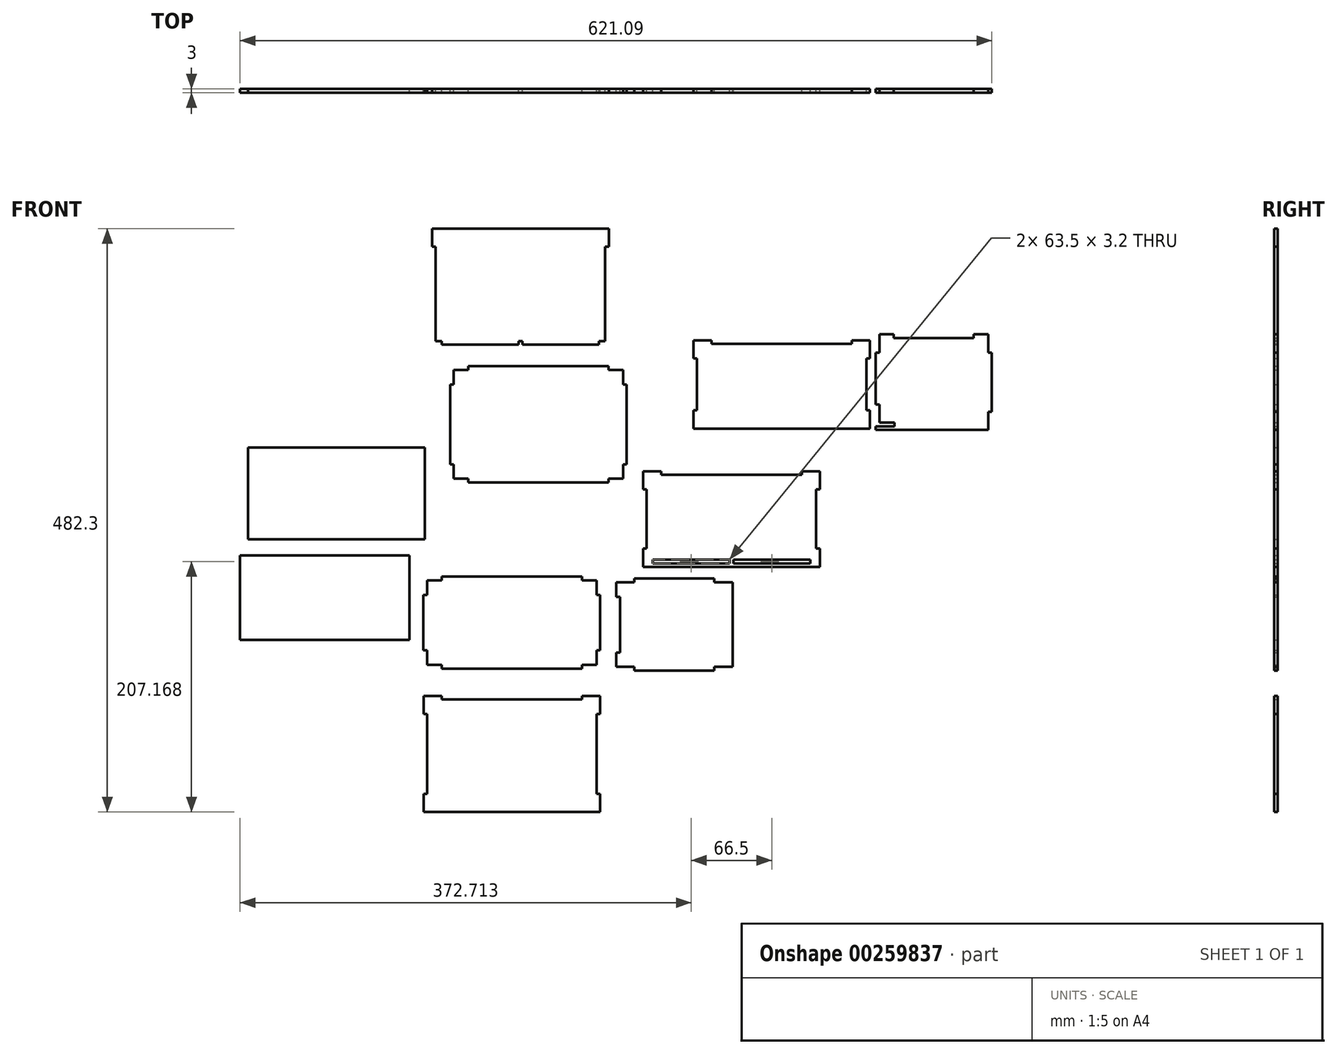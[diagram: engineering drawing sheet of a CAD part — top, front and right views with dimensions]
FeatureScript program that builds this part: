
annotation { "Feature Type Name" : "Feature", "Feature Type Description" : "" }
export const myFeature = defineFeature(function(context is Context, id is Id, definition is map)
    precondition{}
    {
        {
            var Q0;
            Q0=qCreatedBy(makeId("Front.planeOp"),FACE);
            var sketch = newSketch(context, id + "F0", { "sketchPlane" : qUnion([Q0])});
            skLineSegment(sketch, "E0.bottom", {"start": v(-79.7, 20.87) * mm, "end": v(60.3, 20.87) * mm});
            skLineSegment(sketch, "E0.top", {"start": v(-79.7, -49.13) * mm, "end": v(60.3, -49.13) * mm});
            skLineSegment(sketch, "E0.left", {"start": v(-79.7, 20.87) * mm, "end": v(-79.7, -49.13) * mm});
            skLineSegment(sketch, "E0.right", {"start": v(60.3, 20.87) * mm, "end": v(60.3, -49.13) * mm});
            skSolve(sketch);
        }
        {
            var Q0;
            Q0 = qSketchRegion(id + "F0", true);
            extrude(context, id + "F1", {"entities" : qUnion([Q0]), "depth" : 3 * mm});
        }
        {
            var Q0;
            Q0=qCreatedBy(makeId("Front.planeOp"),FACE);
            var sketch = newSketch(context, id + "F2", { "sketchPlane" : qUnion([Q0])});
            skLineSegment(sketch, "E1.bottom", {"start": v(-73.11, 34.1) * mm, "end": v(72.89, 34.1) * mm});
            skLineSegment(sketch, "E1.top", {"start": v(-73.11, 110.1) * mm, "end": v(72.89, 110.1) * mm});
            skLineSegment(sketch, "E1.left", {"start": v(-73.11, 34.1) * mm, "end": v(-73.11, 110.1) * mm});
            skLineSegment(sketch, "E1.right", {"start": v(72.89, 34.1) * mm, "end": v(72.89, 110.1) * mm});
            skSolve(sketch);
        }
        {
            var Q0;
            Q0 = qSketchRegion(id + "F2", true);
            extrude(context, id + "F3", {"entities" : qUnion([Q0]), "depth" : 3 * mm});
        }
        {
            var Q0;
            Q0=qCreatedBy(makeId("Front.planeOp"),FACE);
            var sketch = newSketch(context, id + "F4", { "sketchPlane" : qUnion([Q0])});
            skLineSegment(sketch, "E2.bottom", {"start": v(86.8, 3.27) * mm, "end": v(202.8, 3.27) * mm});
            skLineSegment(sketch, "E2.top", {"start": v(86.8, -72.73) * mm, "end": v(202.8, -72.73) * mm});
            skLineSegment(sketch, "E2.left", {"start": v(71.8, -11.73) * mm, "end": v(71.8, -57.73) * mm});
            skLineSegment(sketch, "E2.right", {"start": v(217.8, -11.73) * mm, "end": v(217.8, -57.73) * mm});
            skLineSegment(sketch, "E3", {"start": v(71.8, -11.73) * mm, "end": v(74.8, -11.73) * mm});
            skLineSegment(sketch, "E4", {"start": v(74.8, -11.73) * mm, "end": v(74.8, 0.27) * mm});
            skLineSegment(sketch, "E5", {"start": v(74.8, 0.27) * mm, "end": v(86.8, 0.27) * mm});
            skLineSegment(sketch, "E6", {"start": v(86.8, 0.27) * mm, "end": v(86.8, 3.27) * mm});
            skLineSegment(sketch, "E7", {"start": v(71.8, -57.73) * mm, "end": v(74.8, -57.73) * mm});
            skLineSegment(sketch, "E8", {"start": v(74.8, -57.73) * mm, "end": v(74.8, -69.73) * mm});
            skLineSegment(sketch, "E9", {"start": v(74.8, -69.73) * mm, "end": v(86.8, -69.73) * mm});
            skLineSegment(sketch, "E10", {"start": v(86.8, -69.73) * mm, "end": v(86.8, -72.73) * mm});
            skLineSegment(sketch, "E11", {"start": v(217.8, -57.73) * mm, "end": v(214.8, -57.73) * mm});
            skLineSegment(sketch, "E12", {"start": v(214.8, -57.73) * mm, "end": v(214.8, -69.73) * mm});
            skLineSegment(sketch, "E13", {"start": v(214.8, -69.73) * mm, "end": v(202.8, -69.73) * mm});
            skLineSegment(sketch, "E14", {"start": v(202.8, -69.73) * mm, "end": v(202.8, -72.73) * mm});
            skLineSegment(sketch, "E15", {"start": v(202.8, 3.27) * mm, "end": v(202.8, 0.27) * mm});
            skLineSegment(sketch, "E16", {"start": v(202.8, 0.27) * mm, "end": v(214.8, 0.27) * mm});
            skLineSegment(sketch, "E17", {"start": v(214.8, 0.27) * mm, "end": v(214.8, -11.73) * mm});
            skLineSegment(sketch, "E18", {"start": v(214.8, -11.73) * mm, "end": v(217.8, -11.73) * mm});
            skSolve(sketch);
        }
        {
            var Q0;
            Q0 = qSketchRegion(id + "F4", true);
            extrude(context, id + "F5", {"entities" : qUnion([Q0]), "depth" : 3 * mm});
        }
        {
            var Q0;
            Q0=qCreatedBy(makeId("Front.planeOp"),FACE);
            var sketch = newSketch(context, id + "F6", { "sketchPlane" : qUnion([Q0])});
            skLineSegment(sketch, "E19.bottom", {"start": v(231.11, -1.34) * mm, "end": v(246.11, -1.34) * mm});
            skLineSegment(sketch, "E19.top", {"start": v(231.11, -71.34) * mm, "end": v(246.11, -71.34) * mm});
            skLineSegment(sketch, "E19.left", {"start": v(231.11, -1.34) * mm, "end": v(231.11, -13.34) * mm});
            skLineSegment(sketch, "E19.right", {"start": v(327.11, -1.34) * mm, "end": v(327.11, -71.34) * mm});
            skLineSegment(sketch, "E20", {"start": v(231.11, -13.34) * mm, "end": v(234.11, -13.34) * mm});
            skLineSegment(sketch, "E21", {"start": v(231.11, -59.34) * mm, "end": v(234.11, -59.34) * mm});
            skLineSegment(sketch, "E22", {"start": v(234.11, -13.34) * mm, "end": v(234.11, -59.34) * mm});
            skLineSegment(sketch, "E23.trimOffspring", {"start": v(231.11, -59.34) * mm, "end": v(231.11, -71.34) * mm});
            skLineSegment(sketch, "E24", {"start": v(246.11, -71.34) * mm, "end": v(246.11, -74.34) * mm});
            skLineSegment(sketch, "E25", {"start": v(246.11, -74.34) * mm, "end": v(312.11, -74.34) * mm});
            skLineSegment(sketch, "E26", {"start": v(312.11, -74.34) * mm, "end": v(312.11, -71.34) * mm});
            skLineSegment(sketch, "E27", {"start": v(246.11, -1.34) * mm, "end": v(246.11, 1.66) * mm});
            skLineSegment(sketch, "E28", {"start": v(246.11, 1.66) * mm, "end": v(312.11, 1.66) * mm});
            skLineSegment(sketch, "E29", {"start": v(312.11, 1.66) * mm, "end": v(312.11, -1.34) * mm});
            skLineSegment(sketch, "E30.trimOffspring", {"start": v(312.11, -1.34) * mm, "end": v(327.11, -1.34) * mm});
            skLineSegment(sketch, "E31.trimOffspring", {"start": v(312.11, -71.34) * mm, "end": v(327.11, -71.34) * mm});
            skSolve(sketch);
        }
        {
            var Q0;
            Q0=makeQuery(id+"F6.imprint","IMPRINT",FACE,{"disambiguationData":[TD([[makeQuery(id+"F6.imprint","IMPRINT",EDGE,{"derivedFrom":sQuery(id+"F6.wireOp",EDGE,"E19.bottom")}),-1.0]])]});
            extrude(context, id + "F7", {"entities" : qUnion([Q0]), "depth" : 3 * mm});
        }
        {
            var Q0;
            Q0=qCreatedBy(makeId("Front.planeOp"),FACE);
            var sketch = newSketch(context, id + "F8", { "sketchPlane" : qUnion([Q0])});
            skLineSegment(sketch, "E32.bottom", {"start": v(71.85, -95.3) * mm, "end": v(86.85, -95.3) * mm});
            skLineSegment(sketch, "E32.top", {"start": v(71.85, -191.3) * mm, "end": v(217.85, -191.3) * mm});
            skLineSegment(sketch, "E32.left", {"start": v(71.85, -95.3) * mm, "end": v(71.85, -110.3) * mm});
            skLineSegment(sketch, "E32.right", {"start": v(217.85, -95.3) * mm, "end": v(217.85, -110.3) * mm});
            skLineSegment(sketch, "E33", {"start": v(86.85, -95.3) * mm, "end": v(86.85, -98.3) * mm});
            skLineSegment(sketch, "E34", {"start": v(86.85, -98.3) * mm, "end": v(202.85, -98.3) * mm});
            skLineSegment(sketch, "E35", {"start": v(202.85, -98.3) * mm, "end": v(202.85, -95.3) * mm});
            skLineSegment(sketch, "E36.trimOffspring", {"start": v(202.85, -95.3) * mm, "end": v(217.85, -95.3) * mm});
            skLineSegment(sketch, "E37", {"start": v(217.85, -110.3) * mm, "end": v(214.85, -110.3) * mm});
            skLineSegment(sketch, "E38", {"start": v(214.85, -110.3) * mm, "end": v(214.85, -176.3) * mm});
            skLineSegment(sketch, "E39", {"start": v(214.85, -176.3) * mm, "end": v(217.85, -176.3) * mm});
            skLineSegment(sketch, "E40", {"start": v(71.85, -110.3) * mm, "end": v(74.85, -110.3) * mm});
            skLineSegment(sketch, "E41", {"start": v(74.85, -110.3) * mm, "end": v(74.85, -176.3) * mm});
            skLineSegment(sketch, "E42", {"start": v(74.85, -176.3) * mm, "end": v(71.85, -176.3) * mm});
            skLineSegment(sketch, "E43.trimOffspring", {"start": v(71.85, -176.3) * mm, "end": v(71.85, -191.3) * mm});
            skLineSegment(sketch, "E44.trimOffspring", {"start": v(217.85, -176.3) * mm, "end": v(217.85, -191.3) * mm});
            skSolve(sketch);
        }
        {
            var Q0;
            Q0 = qSketchRegion(id + "F8", true);
            extrude(context, id + "F9", {"entities" : qUnion([Q0]), "depth" : 3 * mm});
        }
        {
            var Q0;
            Q0=qCreatedBy(makeId("Front.planeOp"),FACE);
            var sketch = newSketch(context, id + "F10", { "sketchPlane" : qUnion([Q0])});
            skLineSegment(sketch, "E45.bottom", {"start": v(108.74, 177.2) * mm, "end": v(224.74, 177.2) * mm});
            skLineSegment(sketch, "E45.top", {"start": v(108.74, 81.2) * mm, "end": v(224.74, 81.2) * mm});
            skLineSegment(sketch, "E45.left", {"start": v(93.74, 162.2) * mm, "end": v(93.74, 96.2) * mm});
            skLineSegment(sketch, "E45.right", {"start": v(239.74, 162.2) * mm, "end": v(239.74, 96.2) * mm});
            skLineSegment(sketch, "E46", {"start": v(93.74, 162.2) * mm, "end": v(96.74, 162.2) * mm});
            skLineSegment(sketch, "E47", {"start": v(96.74, 162.2) * mm, "end": v(96.74, 174.2) * mm});
            skLineSegment(sketch, "E48", {"start": v(96.74, 174.2) * mm, "end": v(108.74, 174.2) * mm});
            skLineSegment(sketch, "E49", {"start": v(108.74, 174.2) * mm, "end": v(108.74, 177.2) * mm});
            skLineSegment(sketch, "E50", {"start": v(93.74, 96.2) * mm, "end": v(96.74, 96.2) * mm});
            skLineSegment(sketch, "E51", {"start": v(96.74, 96.2) * mm, "end": v(96.74, 84.2) * mm});
            skLineSegment(sketch, "E52", {"start": v(96.74, 84.2) * mm, "end": v(108.74, 84.2) * mm});
            skLineSegment(sketch, "E53", {"start": v(108.74, 84.2) * mm, "end": v(108.74, 81.2) * mm});
            skLineSegment(sketch, "E54", {"start": v(239.74, 96.2) * mm, "end": v(236.74, 96.2) * mm});
            skLineSegment(sketch, "E55", {"start": v(236.74, 96.2) * mm, "end": v(236.74, 84.2) * mm});
            skLineSegment(sketch, "E56", {"start": v(236.74, 84.2) * mm, "end": v(224.74, 84.2) * mm});
            skLineSegment(sketch, "E57", {"start": v(224.74, 84.2) * mm, "end": v(224.74, 81.2) * mm});
            skLineSegment(sketch, "E58", {"start": v(224.74, 177.2) * mm, "end": v(224.74, 174.2) * mm});
            skLineSegment(sketch, "E59", {"start": v(224.74, 174.2) * mm, "end": v(236.74, 174.2) * mm});
            skLineSegment(sketch, "E60", {"start": v(236.74, 174.2) * mm, "end": v(236.74, 162.2) * mm});
            skLineSegment(sketch, "E61", {"start": v(236.74, 162.2) * mm, "end": v(239.74, 162.2) * mm});
            skSolve(sketch);
        }
        {
            var Q0;
            Q0=makeQuery(id+"F10.imprint","IMPRINT",FACE,{"disambiguationData":[TD([[makeQuery(id+"F10.imprint","IMPRINT",EDGE,{"derivedFrom":sQuery(id+"F10.wireOp",EDGE,"E45.bottom")}),-1.0]])]});
            extrude(context, id + "F11", {"entities" : qUnion([Q0]), "depth" : 3 * mm});
        }
        {
            var Q0;
            Q0=qCreatedBy(makeId("Front.planeOp"),FACE);
            var sketch = newSketch(context, id + "F12", { "sketchPlane" : qUnion([Q0])});
            skLineSegment(sketch, "E62.bottom", {"start": v(253.26, 90.46) * mm, "end": v(268.26, 90.46) * mm});
            skLineSegment(sketch, "E62.top", {"start": v(253.26, 11.46) * mm, "end": v(399.26, 11.46) * mm});
            skLineSegment(sketch, "E62.left", {"start": v(253.26, 90.46) * mm, "end": v(253.26, 75.46) * mm});
            skLineSegment(sketch, "E62.right", {"start": v(399.26, 90.46) * mm, "end": v(399.26, 75.46) * mm});
            skLineSegment(sketch, "E63", {"start": v(268.26, 90.46) * mm, "end": v(268.26, 87.46) * mm});
            skLineSegment(sketch, "E64", {"start": v(268.26, 87.46) * mm, "end": v(384.26, 87.46) * mm});
            skLineSegment(sketch, "E65", {"start": v(384.26, 87.46) * mm, "end": v(384.26, 90.46) * mm});
            skLineSegment(sketch, "E66", {"start": v(399.26, 75.46) * mm, "end": v(396.26, 75.46) * mm});
            skLineSegment(sketch, "E67", {"start": v(396.26, 75.46) * mm, "end": v(396.26, 26.46) * mm});
            skLineSegment(sketch, "E68", {"start": v(396.26, 26.46) * mm, "end": v(399.26, 26.46) * mm});
            skLineSegment(sketch, "E69", {"start": v(253.26, 75.46) * mm, "end": v(256.26, 75.46) * mm});
            skLineSegment(sketch, "E70", {"start": v(256.26, 75.46) * mm, "end": v(256.26, 26.46) * mm});
            skLineSegment(sketch, "E71", {"start": v(256.26, 26.46) * mm, "end": v(253.26, 26.46) * mm});
            skLineSegment(sketch, "E72.trimOffspring", {"start": v(384.26, 90.46) * mm, "end": v(399.26, 90.46) * mm});
            skLineSegment(sketch, "E73.trimOffspring", {"start": v(253.26, 26.46) * mm, "end": v(253.26, 11.46) * mm});
            skLineSegment(sketch, "E74.trimOffspring", {"start": v(399.26, 26.46) * mm, "end": v(399.26, 11.46) * mm});
            skLineSegment(sketch, "E75.bottom", {"start": v(261.26, 17.46) * mm, "end": v(324.76, 17.46) * mm});
            skLineSegment(sketch, "E75.top", {"start": v(261.26, 14.26) * mm, "end": v(324.76, 14.26) * mm});
            skLineSegment(sketch, "E75.left", {"start": v(261.26, 17.46) * mm, "end": v(261.26, 14.26) * mm});
            skLineSegment(sketch, "E75.right", {"start": v(324.76, 17.46) * mm, "end": v(324.76, 14.26) * mm});
            skLineSegment(sketch, "E76.bottom", {"start": v(327.76, 17.46) * mm, "end": v(391.26, 17.46) * mm});
            skLineSegment(sketch, "E76.top", {"start": v(327.76, 14.26) * mm, "end": v(391.26, 14.26) * mm});
            skLineSegment(sketch, "E76.left", {"start": v(327.76, 17.46) * mm, "end": v(327.76, 14.26) * mm});
            skLineSegment(sketch, "E76.right", {"start": v(391.26, 17.46) * mm, "end": v(391.26, 14.26) * mm});
            skSolve(sketch);
        }
        {
            var Q0;
            Q0=makeQuery(id+"F12.imprint","IMPRINT",FACE,{"disambiguationData":[TD([[makeQuery(id+"F12.imprint","IMPRINT",EDGE,{"derivedFrom":sQuery(id+"F12.wireOp",EDGE,"E62.bottom")}),-1.0]])]});
            extrude(context, id + "F13", {"entities" : qUnion([Q0]), "depth" : 3 * mm});
        }
        {
            var Q0;
            Q0=qCreatedBy(makeId("Front.planeOp"),FACE);
            var sketch = newSketch(context, id + "F14", { "sketchPlane" : qUnion([Q0])});
            skLineSegment(sketch, "E77.bottom", {"start": v(294.72, 125.74) * mm, "end": v(440.72, 125.74) * mm});
            skLineSegment(sketch, "E77.top", {"start": v(294.72, 198.74) * mm, "end": v(309.72, 198.74) * mm});
            skLineSegment(sketch, "E77.left", {"start": v(294.72, 125.74) * mm, "end": v(294.72, 140.74) * mm});
            skLineSegment(sketch, "E77.right", {"start": v(440.72, 125.74) * mm, "end": v(440.72, 140.74) * mm});
            skLineSegment(sketch, "E78", {"start": v(309.72, 198.74) * mm, "end": v(309.72, 195.74) * mm});
            skLineSegment(sketch, "E79", {"start": v(309.72, 195.74) * mm, "end": v(425.72, 195.74) * mm});
            skLineSegment(sketch, "E80", {"start": v(425.72, 195.74) * mm, "end": v(425.72, 198.74) * mm});
            skLineSegment(sketch, "E81", {"start": v(440.72, 183.74) * mm, "end": v(437.72, 183.74) * mm});
            skLineSegment(sketch, "E82", {"start": v(437.72, 183.74) * mm, "end": v(437.72, 140.74) * mm});
            skLineSegment(sketch, "E83", {"start": v(437.72, 140.74) * mm, "end": v(440.72, 140.74) * mm});
            skLineSegment(sketch, "E84", {"start": v(294.72, 183.74) * mm, "end": v(297.72, 183.74) * mm});
            skLineSegment(sketch, "E85", {"start": v(297.72, 183.74) * mm, "end": v(297.72, 140.74) * mm});
            skLineSegment(sketch, "E86", {"start": v(297.72, 140.74) * mm, "end": v(294.72, 140.74) * mm});
            skLineSegment(sketch, "E87.trimOffspring", {"start": v(425.72, 198.74) * mm, "end": v(440.72, 198.74) * mm});
            skLineSegment(sketch, "E88.trimOffspring", {"start": v(294.72, 183.74) * mm, "end": v(294.72, 198.74) * mm});
            skLineSegment(sketch, "E89.trimOffspring", {"start": v(440.72, 183.74) * mm, "end": v(440.72, 198.74) * mm});
            skSolve(sketch);
        }
        {
            var Q0;
            Q0 = qSketchRegion(id + "F14", true);
            extrude(context, id + "F15", {"entities" : qUnion([Q0]), "depth" : 3 * mm});
        }
        {
            var Q0;
            Q0=qCreatedBy(makeId("Front.planeOp"),FACE);
            var sketch = newSketch(context, id + "F16", { "sketchPlane" : qUnion([Q0])});
            skLineSegment(sketch, "E90.bottom", {"start": v(448.4, 203.6) * mm, "end": v(460.4, 203.6) * mm});
            skLineSegment(sketch, "E90.left", {"start": v(445.4, 188.6) * mm, "end": v(445.4, 145.6) * mm});
            skLineSegment(sketch, "E90.right", {"start": v(541.4, 188.6) * mm, "end": v(541.4, 139.6) * mm});
            skLineSegment(sketch, "E91", {"start": v(445.4, 188.6) * mm, "end": v(448.4, 188.6) * mm});
            skLineSegment(sketch, "E92", {"start": v(448.4, 188.6) * mm, "end": v(448.4, 203.6) * mm});
            skLineSegment(sketch, "E93", {"start": v(445.4, 145.6) * mm, "end": v(448.4, 145.6) * mm});
            skLineSegment(sketch, "E94", {"start": v(448.4, 145.6) * mm, "end": v(448.4, 130.6) * mm});
            skLineSegment(sketch, "E95", {"start": v(460.4, 203.6) * mm, "end": v(460.4, 200.6) * mm});
            skLineSegment(sketch, "E96", {"start": v(460.4, 200.6) * mm, "end": v(526.4, 200.6) * mm});
            skLineSegment(sketch, "E97", {"start": v(526.4, 200.6) * mm, "end": v(526.4, 203.6) * mm});
            skLineSegment(sketch, "E98", {"start": v(541.4, 188.6) * mm, "end": v(538.4, 188.6) * mm});
            skLineSegment(sketch, "E99", {"start": v(538.4, 188.6) * mm, "end": v(538.4, 203.6) * mm});
            skLineSegment(sketch, "E100", {"start": v(541.4, 139.6) * mm, "end": v(538.4, 139.6) * mm});
            skLineSegment(sketch, "E101", {"start": v(538.4, 139.6) * mm, "end": v(538.4, 124.6) * mm});
            skLineSegment(sketch, "E102.trimOffspring", {"start": v(526.4, 203.6) * mm, "end": v(538.4, 203.6) * mm});
            skPoint(sketch, "E103.orphan", {"position": v(541.4, 124.6) * mm});
            skLineSegment(sketch, "E104", {"start": v(445.4, 124.6) * mm, "end": v(445.4, 127.4) * mm});
            skLineSegment(sketch, "E105", {"start": v(445.4, 127.4) * mm, "end": v(460.8, 127.4) * mm});
            skLineSegment(sketch, "E106", {"start": v(448.4, 130.6) * mm, "end": v(460.77, 130.6) * mm});
            skLineSegment(sketch, "E107", {"start": v(460.77, 130.6) * mm, "end": v(460.8, 127.4) * mm});
            skLineSegment(sketch, "E108", {"start": v(538.4, 124.6) * mm, "end": v(445.4, 124.6) * mm});
            skSolve(sketch);
        }
        {
            var Q0;
            Q0 = qSketchRegion(id + "F16", true);
            extrude(context, id + "F17", {"entities" : qUnion([Q0]), "depth" : 3 * mm});
        }
        {
            var Q0;
            Q0=qCreatedBy(makeId("Front.planeOp"),FACE);
            var sketch = newSketch(context, id + "F18", { "sketchPlane" : qUnion([Q0])});
            skLineSegment(sketch, "E109.bottom", {"start": v(78.94, 291) * mm, "end": v(224.94, 291) * mm});
            skLineSegment(sketch, "E109.top", {"start": v(87.04, 195) * mm, "end": v(150.34, 195) * mm});
            skLineSegment(sketch, "E109.left", {"start": v(78.94, 291) * mm, "end": v(78.94, 276) * mm});
            skLineSegment(sketch, "E110", {"start": v(78.94, 276) * mm, "end": v(81.94, 276) * mm});
            skLineSegment(sketch, "E111", {"start": v(81.94, 276) * mm, "end": v(81.94, 198) * mm});
            skLineSegment(sketch, "E112", {"start": v(81.94, 198) * mm, "end": v(87.04, 198) * mm});
            skLineSegment(sketch, "E113", {"start": v(87.04, 198) * mm, "end": v(87.04, 195) * mm});
            skLineSegment(sketch, "E114", {"start": v(224.94, 276) * mm, "end": v(221.94, 276) * mm});
            skLineSegment(sketch, "E115", {"start": v(221.94, 276) * mm, "end": v(221.94, 198) * mm});
            skLineSegment(sketch, "E116", {"start": v(221.94, 198) * mm, "end": v(216.84, 198) * mm});
            skLineSegment(sketch, "E117", {"start": v(216.84, 198) * mm, "end": v(216.84, 195) * mm});
            skLineSegment(sketch, "E118", {"start": v(150.34, 195) * mm, "end": v(150.34, 198) * mm});
            skLineSegment(sketch, "E119", {"start": v(150.34, 198) * mm, "end": v(153.54, 198) * mm});
            skLineSegment(sketch, "E120", {"start": v(153.54, 198) * mm, "end": v(153.54, 195) * mm});
            skLineSegment(sketch, "E121", {"start": v(224.94, 276) * mm, "end": v(224.94, 291) * mm});
            skLineSegment(sketch, "E122", {"start": v(153.54, 195) * mm, "end": v(216.84, 195) * mm});
            skSolve(sketch);
        }
        {
            var Q0;
            Q0=makeQuery(id+"F18.imprint","IMPRINT",FACE,{"disambiguationData":[TD([[makeQuery(id+"F18.imprint","IMPRINT",EDGE,{"derivedFrom":sQuery(id+"F18.wireOp",EDGE,"E109.bottom")}),-1.0]])]});
            extrude(context, id + "F19", {"entities" : qUnion([Q0]), "depth" : 3 * mm});
        }
    });
